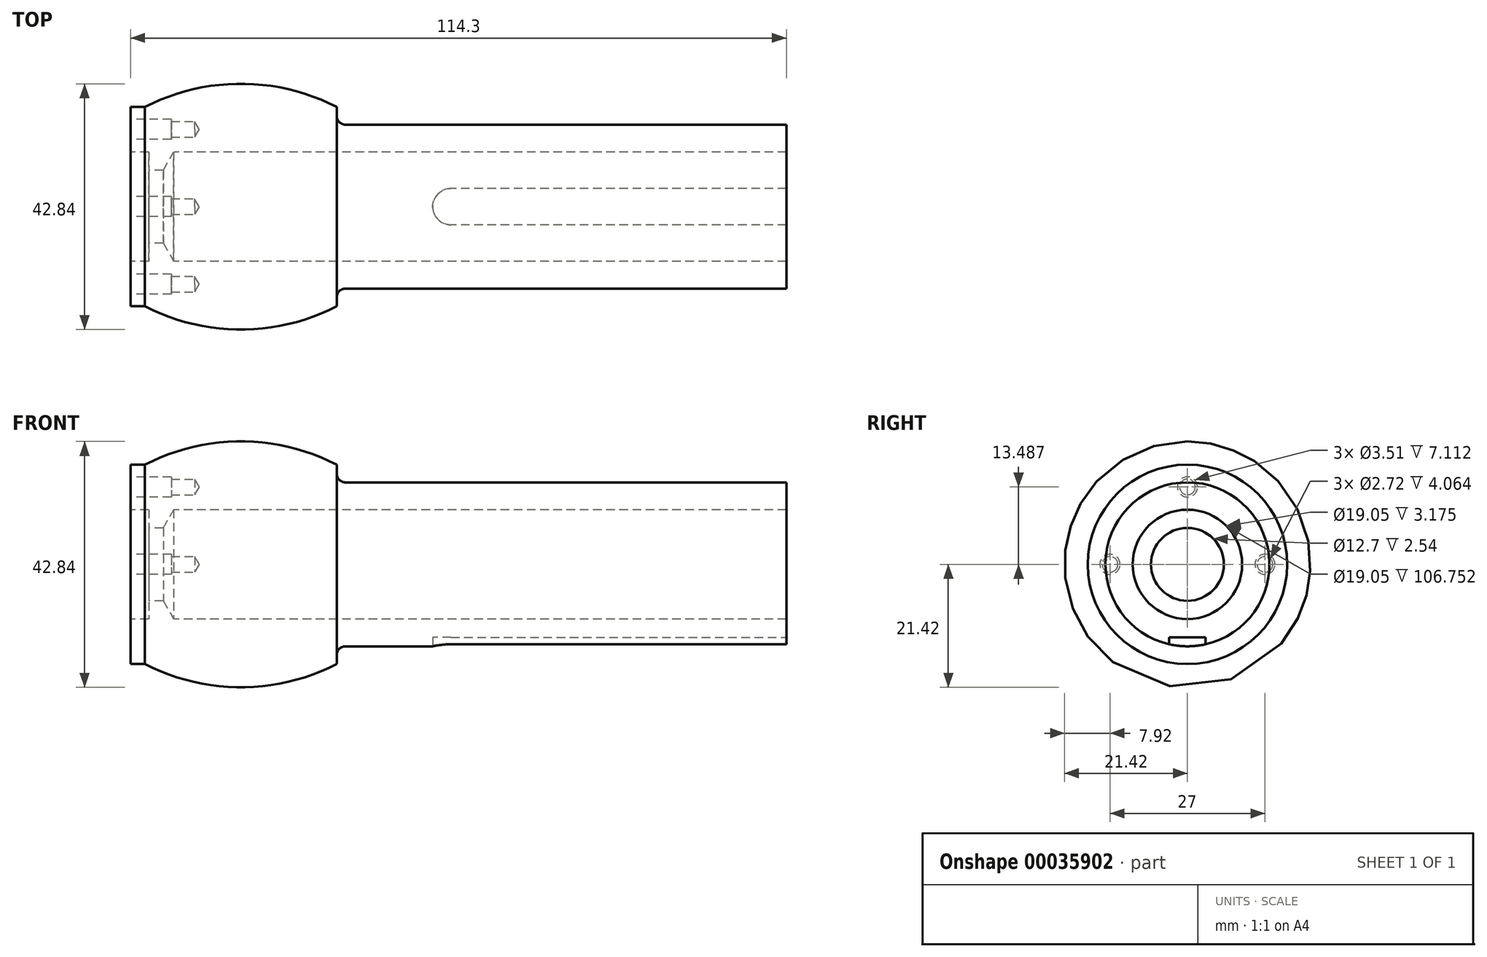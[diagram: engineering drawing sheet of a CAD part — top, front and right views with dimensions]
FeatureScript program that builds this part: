
annotation { "Feature Type Name" : "Feature", "Feature Type Description" : "" }
export const myFeature = defineFeature(function(context is Context, id is Id, definition is map)
    precondition{}
    {
        {
            var Q0;
            Q0=qCreatedBy(makeId("Front.planeOp"),FACE);
            var sketch = newSketch(context, id + "F0", { "sketchPlane" : qUnion([Q0])});
            skLineSegment(sketch, "E0", {"start": v(0, 0) * mm, "end": v(114.3, 0) * mm, "construction": true});
            skLineSegment(sketch, "E1", {"start": v(2.51, 17.37) * mm, "end": v(0, 17.37) * mm});
            skLineSegment(sketch, "E2", {"start": v(0, 17.37) * mm, "end": v(0, 9.52) * mm});
            skLineSegment(sketch, "E3", {"start": v(0, 9.52) * mm, "end": v(3.18, 9.52) * mm});
            skLineSegment(sketch, "E4", {"start": v(3.18, 9.52) * mm, "end": v(3.18, 6.35) * mm});
            skLineSegment(sketch, "E5", {"start": v(3.18, 6.35) * mm, "end": v(5.72, 6.35) * mm});
            skLineSegment(sketch, "E6", {"start": v(5.71, 6.35) * mm, "end": v(7.55, 9.53) * mm});
            skLineSegment(sketch, "E7", {"start": v(7.55, 9.52) * mm, "end": v(114.3, 9.53) * mm});
            skLineSegment(sketch, "E8", {"start": v(114.3, 9.53) * mm, "end": v(114.3, 14.29) * mm});
            skLineSegment(sketch, "E9", {"start": v(114.3, 14.29) * mm, "end": v(35.94, 14.29) * mm});
            skLineSegment(sketch, "E10", {"start": v(35.94, 14.29) * mm, "end": v(35.94, 17.37) * mm});
            skArc(sketch, "E11", {"start": v(35.94, 17.37) * mm, "mid": v(19.23, 21.42) * mm, "end": v(2.51, 17.37) * mm});
            skSolve(sketch);
        }
        {
            var Q0;
            Q0=makeQuery(id+"F0.imprint","IMPRINT",FACE,{"disambiguationData":[TD([[makeQuery(id+"F0.imprint","IMPRINT",EDGE,{"derivedFrom":sQuery(id+"F0.wireOp",EDGE,"E1")}),1.0]])]});
            var Q1;
            Q1=sQuery(id+"F0.wireOp",EDGE,"E0");
            revolve(context, id + "F1", {"entities" : qUnion([Q0]), "axis" : qUnion([Q1]), "revolveType" : RevolveType.FULL});
        }
        {
            var Q0;
            Q0=makeQuery(id+"F1.opRevolve","SWEPT_FACE",FACE,{"disambiguationData":[OSD([sQuery(id+"F0.wireOp",EDGE,"E2")])]});
            var sketch = newSketch(context, id + "F2", { "sketchPlane" : qUnion([Q0])});
            skCircle(sketch, "E12", {"center": v(0, 13.49) * mm, "radius": 1.75 * mm});
            skCircle(sketch, "E13", {"center": v(-13.5, 0) * mm, "radius": 1.75 * mm});
            skCircle(sketch, "E14", {"center": v(13.5, 0) * mm, "radius": 1.75 * mm});
            skLineSegment(sketch, "E15", {"start": v(-13.5, 0) * mm, "end": v(13.5, 0) * mm, "construction": true});
            skSolve(sketch);
        }
        {
            var Q0;
            Q0=sQuery(id+"F2.wireOp",VERTEX,"E13.center");
            var Q1;
            Q1=sQuery(id+"F2.wireOp",VERTEX,"E12.center");
            var Q2;
            Q2=sQuery(id+"F2.wireOp",VERTEX,"E14.center");
            var Q3;
            Q3=makeQuery(id+"F1.opRevolve","SWEPT_BODY",BODY,{"disambiguationData":[OSD([sQuery(id+"F0.wireOp",EDGE,"E1"),sQuery(id+"F0.wireOp",EDGE,"E2"),sQuery(id+"F0.wireOp",EDGE,"E3"),sQuery(id+"F0.wireOp",EDGE,"E4"),sQuery(id+"F0.wireOp",EDGE,"E5"),sQuery(id+"F0.wireOp",EDGE,"E6"),sQuery(id+"F0.wireOp",EDGE,"E7"),sQuery(id+"F0.wireOp",EDGE,"E8"),sQuery(id+"F0.wireOp",EDGE,"E9"),sQuery(id+"F0.wireOp",EDGE,"E10"),sQuery(id+"F0.wireOp",EDGE,"E11")])]});
            hole(context, id + "F3", {"style" : HoleStyle.SIMPLE, "holeDiameter" : 2.72 * mm, "endStyle" : HoleEndStyle.BLIND, "holeDepth" : 11.18 * mm, "locations" : qUnion([Q0, Q1, Q2]), "scope" : qUnion([Q3])});
        }
        {
            var Q0;
            Q0=makeQuery(id+"F2.imprint","IMPRINT",FACE,{"disambiguationData":[TD([[makeQuery(id+"F2.imprint","IMPRINT",EDGE,{"derivedFrom":sQuery(id+"F2.wireOp",EDGE,"E13")}),1.0]])]});
            var Q1;
            Q1=makeQuery(id+"F2.imprint","IMPRINT",FACE,{"disambiguationData":[TD([[makeQuery(id+"F2.imprint","IMPRINT",EDGE,{"derivedFrom":sQuery(id+"F2.wireOp",EDGE,"E12")}),1.0]])]});
            var Q2;
            Q2=makeQuery(id+"F2.imprint","IMPRINT",FACE,{"disambiguationData":[TD([[makeQuery(id+"F2.imprint","IMPRINT",EDGE,{"derivedFrom":sQuery(id+"F2.wireOp",EDGE,"E14")}),1.0]])]});
            extrude(context, id + "F4", {"entities" : qUnion([Q0, Q1, Q2]), "operationType" : NewBodyOperationType.REMOVE, "oppositeDirection" : true, "depth" : 7.11 * mm});
        }
        {
            var Q0;
            Q0=makeQuery(id+"F1.opRevolve","SWEPT_FACE",FACE,{"disambiguationData":[OSD([sQuery(id+"F0.wireOp",EDGE,"E8")])]});
            var sketch = newSketch(context, id + "F5", { "sketchPlane" : qUnion([Q0])});
            skCircle(sketch, "E16.0", {"center": v(0, 0) * mm, "radius": 14.29 * mm});
            skPoint(sketch, "E17", {"position": v(0, -14.29) * mm});
            skSolve(sketch);
        }
        {
            var Q0;
            Q0=qCreatedBy(makeId("Top.planeOp"),FACE);
            var Q1;
            Q1=sQuery(id+"F5.wireOp",VERTEX,"E17");
            cPlane(context, id + "F6", {"entities" : qUnion([Q0, Q1]), "cplaneType" : CPlaneType.PLANE_POINT, "offset" : 152.4 * mm, "width" : 152.4 * mm, "height" : 152.4 * mm});
        }
        {
            var Q0;
            Q0=qCreatedBy(id+"F6.planeOp",FACE);
            var sketch = newSketch(context, id + "F7", { "sketchPlane" : qUnion([Q0])});
            skPoint(sketch, "E18.0", {"position": v(114.3, 0) * mm});
            skLineSegment(sketch, "E19", {"start": v(114.3, -3.18) * mm, "end": v(114.3, 3.18) * mm});
            skLineSegment(sketch, "E20", {"start": v(114.3, 3.18) * mm, "end": v(55.85, 3.17) * mm});
            skLineSegment(sketch, "E21", {"start": v(55.85, -3.18) * mm, "end": v(114.3, -3.18) * mm});
            skArc(sketch, "E22", {"start": v(55.85, -3.18) * mm, "mid": v(52.68, 0) * mm, "end": v(55.85, 3.18) * mm});
            skSolve(sketch);
        }
        {
            var Q0;
            Q0=makeQuery(id+"F7.imprint","IMPRINT",FACE,{"disambiguationData":[TD([[makeQuery(id+"F7.imprint","IMPRINT",EDGE,{"derivedFrom":sQuery(id+"F7.wireOp",EDGE,"E19")}),1.0]])]});
            extrude(context, id + "F8", {"entities" : qUnion([Q0]), "operationType" : NewBodyOperationType.REMOVE, "depth" : 1.57 * mm});
        }
        {
            var Q0;
            Q0=makeQuery(id+"F1.opRevolve","SWEPT_EDGE",EDGE,{"disambiguationData":[OSD([sQuery(id+"F0.wireOp",EDGE,"E9"),sQuery(id+"F0.wireOp",EDGE,"E10")])]});
            fillet(context, id + "F9", {"entities" : qUnion([Q0]), "radius" : 1.52 * mm, "tangentPropagation" : true, "allowEdgeOverflow" : false});
        }
    });
